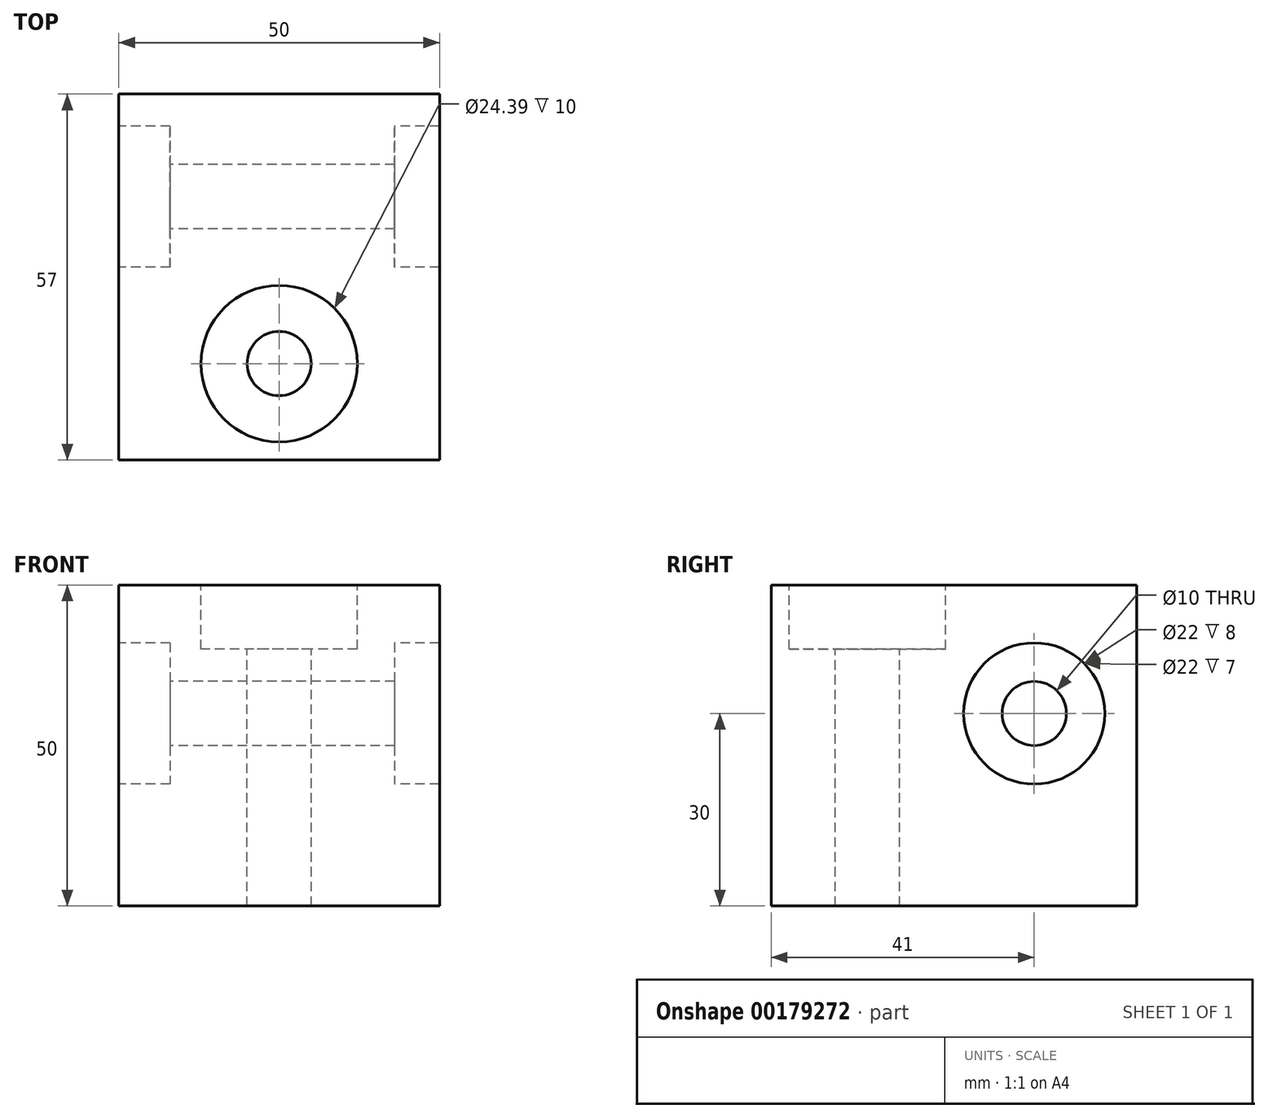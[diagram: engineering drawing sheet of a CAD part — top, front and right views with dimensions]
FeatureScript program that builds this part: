
annotation { "Feature Type Name" : "Feature", "Feature Type Description" : "" }
export const myFeature = defineFeature(function(context is Context, id is Id, definition is map)
    precondition{}
    {
        {
            var Q0;
            Q0=qCreatedBy(makeId("Top.planeOp"),FACE);
            var sketch = newSketch(context, id + "F0", { "sketchPlane" : qUnion([Q0])});
            skLineSegment(sketch, "E0.bottom", {"start": v(0, 0) * mm, "end": v(50, 0) * mm});
            skLineSegment(sketch, "E0.top", {"start": v(0, 57) * mm, "end": v(50, 57) * mm});
            skLineSegment(sketch, "E0.left", {"start": v(0, 0) * mm, "end": v(0, 57) * mm});
            skLineSegment(sketch, "E0.right", {"start": v(50, 0) * mm, "end": v(50, 57) * mm});
            skSolve(sketch);
        }
        {
            var Q0;
            Q0=makeQuery(id+"F0.imprint","IMPRINT",FACE,{"disambiguationData":[TD([[makeQuery(id+"F0.imprint","IMPRINT",EDGE,{"derivedFrom":sQuery(id+"F0.wireOp",EDGE,"E0.bottom")}),1.0]])]});
            extrude(context, id + "F1", {"entities" : qUnion([Q0]), "depth" : 50 * mm});
        }
        {
            var Q0;
            Q0=makeQuery(id+"F1.opExtrude","CAP_FACE",FACE,{"disambiguationData":[OSD([sQuery(id+"F0.wireOp",EDGE,"E0.bottom"),sQuery(id+"F0.wireOp",EDGE,"E0.top"),sQuery(id+"F0.wireOp",EDGE,"E0.left"),sQuery(id+"F0.wireOp",EDGE,"E0.right")])],"isStart":false});
            var sketch = newSketch(context, id + "F2", { "sketchPlane" : qUnion([Q0])});
            skLineSegment(sketch, "E1", {"start": v(25, 0) * mm, "end": v(25, 57) * mm, "construction": true});
            skCircle(sketch, "E2", {"center": v(25, 15) * mm, "radius": 5 * mm});
            skCircle(sketch, "E3", {"center": v(25, 15) * mm, "radius": 12.2 * mm});
            skSolve(sketch);
        }
        {
            var Q0;
            Q0=makeQuery(id+"F2.imprint","IMPRINT",FACE,{"disambiguationData":[TD([[makeQuery(id+"F2.imprint","IMPRINT",EDGE,{"derivedFrom":sQuery(id+"F2.wireOp",EDGE,"E2")}),1.0]])]});
            extrude(context, id + "F3", {"entities" : qUnion([Q0]), "operationType" : NewBodyOperationType.REMOVE, "endBound" : BoundingType.THROUGH_ALL, "oppositeDirection" : true, "depth" : 25 * mm});
        }
        {
            var Q0;
            Q0=makeQuery(id+"F1.opExtrude","SWEPT_FACE",FACE,{"disambiguationData":[OSD([sQuery(id+"F0.wireOp",EDGE,"E0.left")])]});
            var sketch = newSketch(context, id + "F4", { "sketchPlane" : qUnion([Q0])});
            skLineSegment(sketch, "E4", {"start": v(-57, 30) * mm, "end": v(0, 30) * mm, "construction": true});
            skCircle(sketch, "E5", {"center": v(-41, 30) * mm, "radius": 5 * mm});
            skCircle(sketch, "E6", {"center": v(-41, 30) * mm, "radius": 11 * mm});
            skSolve(sketch);
        }
        {
            var Q0;
            Q0=makeQuery(id+"F4.imprint","IMPRINT",FACE,{"disambiguationData":[TD([[makeQuery(id+"F4.imprint","IMPRINT",EDGE,{"derivedFrom":sQuery(id+"F4.wireOp",EDGE,"E5")}),1.0]])]});
            extrude(context, id + "F5", {"entities" : qUnion([Q0]), "operationType" : NewBodyOperationType.REMOVE, "endBound" : BoundingType.THROUGH_ALL, "oppositeDirection" : true, "depth" : 25 * mm});
        }
        {
            var Q0;
            Q0=makeQuery(id+"F4.imprint","IMPRINT",FACE,{"disambiguationData":[TD([[makeQuery(id+"F4.imprint","IMPRINT",EDGE,{"derivedFrom":sQuery(id+"F4.wireOp",EDGE,"E5")}),-1.0]])]});
            extrude(context, id + "F6", {"entities" : qUnion([Q0]), "operationType" : NewBodyOperationType.REMOVE, "oppositeDirection" : true, "depth" : 8 * mm});
        }
        {
            var Q0;
            Q0=makeQuery(id+"F4.imprint","IMPRINT",FACE,{"disambiguationData":[TD([[makeQuery(id+"F4.imprint","IMPRINT",EDGE,{"derivedFrom":sQuery(id+"F4.wireOp",EDGE,"E5")}),-1.0]])]});
            var Q1;
            Q1=makeQuery(id+"F1.opExtrude","SWEPT_FACE",FACE,{"disambiguationData":[OSD([sQuery(id+"F0.wireOp",EDGE,"E0.right")])]});
            extrude(context, id + "F7", {"entities" : qUnion([Q0]), "operationType" : NewBodyOperationType.REMOVE, "endBound" : BoundingType.UP_TO_SURFACE, "oppositeDirection" : true, "endBoundEntityFace" : qUnion([Q1]), "depth" : 49.1 * mm, "hasSecondDirection" : true, "secondDirectionOppositeDirection" : true, "secondDirectionDepth" : 43 * mm});
        }
        {
            var Q0;
            Q0=makeQuery(id+"F2.imprint","IMPRINT",FACE,{"disambiguationData":[TD([[makeQuery(id+"F2.imprint","IMPRINT",EDGE,{"derivedFrom":sQuery(id+"F2.wireOp",EDGE,"E2")}),-1.0]])]});
            extrude(context, id + "F8", {"entities" : qUnion([Q0]), "operationType" : NewBodyOperationType.REMOVE, "oppositeDirection" : true, "depth" : 10 * mm});
        }
    });
